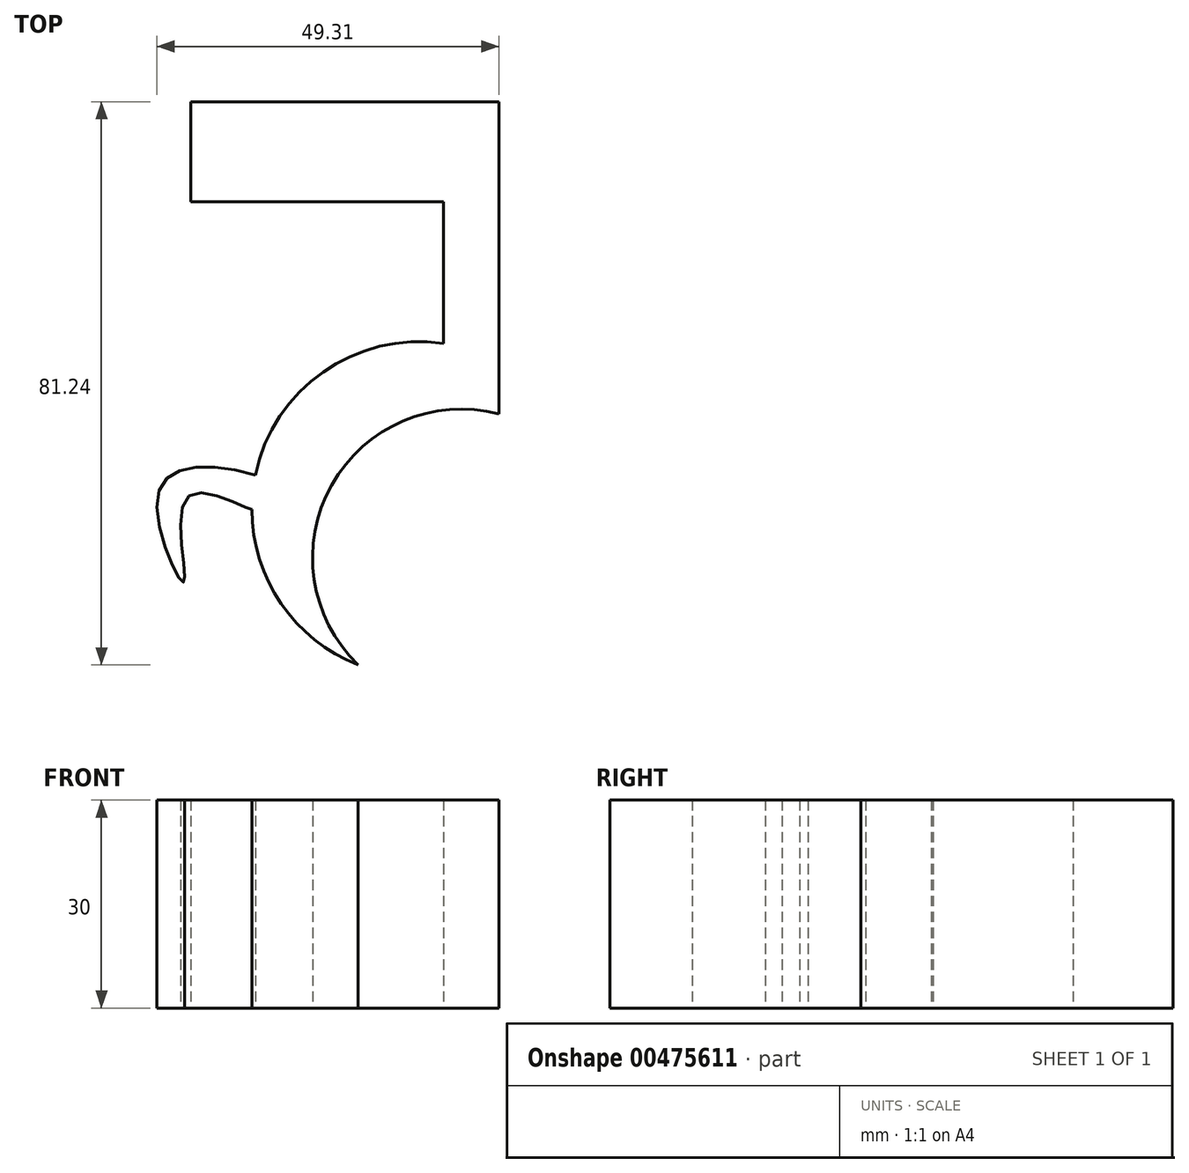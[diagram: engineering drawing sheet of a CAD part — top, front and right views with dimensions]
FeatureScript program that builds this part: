
annotation { "Feature Type Name" : "Feature", "Feature Type Description" : "" }
export const myFeature = defineFeature(function(context is Context, id is Id, definition is map)
    precondition{}
    {
        {
            var Q0;
            Q0=qCreatedBy(makeId("Top.planeOp"),FACE);
            var sketch = newSketch(context, id + "F0", { "sketchPlane" : qUnion([Q0])});
            skLineSegment(sketch, "E0", {"start": v(-22.81, 34.86) * mm, "end": v(21.65, 34.86) * mm});
            skLineSegment(sketch, "E1", {"start": v(-22.81, 34.86) * mm, "end": v(-22.81, 20.43) * mm});
            skLineSegment(sketch, "E2", {"start": v(-22.81, 20.43) * mm, "end": v(13.65, 20.43) * mm});
            skLineSegment(sketch, "E3", {"start": v(21.65, 34.86) * mm, "end": v(21.65, -10.17) * mm});
            skLineSegment(sketch, "E4", {"start": v(13.65, 20.43) * mm, "end": v(13.65, 0) * mm});
            skArc(sketch, "E5", {"start": v(13.65, 0) * mm, "mid": v(-13.18, -17.7) * mm, "end": v(1.34, -46.38) * mm});
            skArc(sketch, "E6", {"start": v(21.65, -10.17) * mm, "mid": v(-2.47, -20.44) * mm, "end": v(1.34, -46.38) * mm});
            skFitSpline(sketch, "E7", {"points": [v(-13.48, -19.01) * mm, v(-27.47, -21.64) * mm, v(-23.76, -34.43) * mm, v(-23.05, -22) * mm, v(-13.98, -23.98) * mm, v(-13.98, -23.7) * mm], "startDerivative": vector(-69.5, 21.66) * mm, "endDerivative": vector(-3.98, 8.91) * mm});
            skSolve(sketch);
        }
        {
            var Q0;
            Q0 = qSketchRegion(id + "F0", true);
            extrude(context, id + "F1", {"entities" : qUnion([Q0]), "depth" : 30 * mm});
        }
    });
